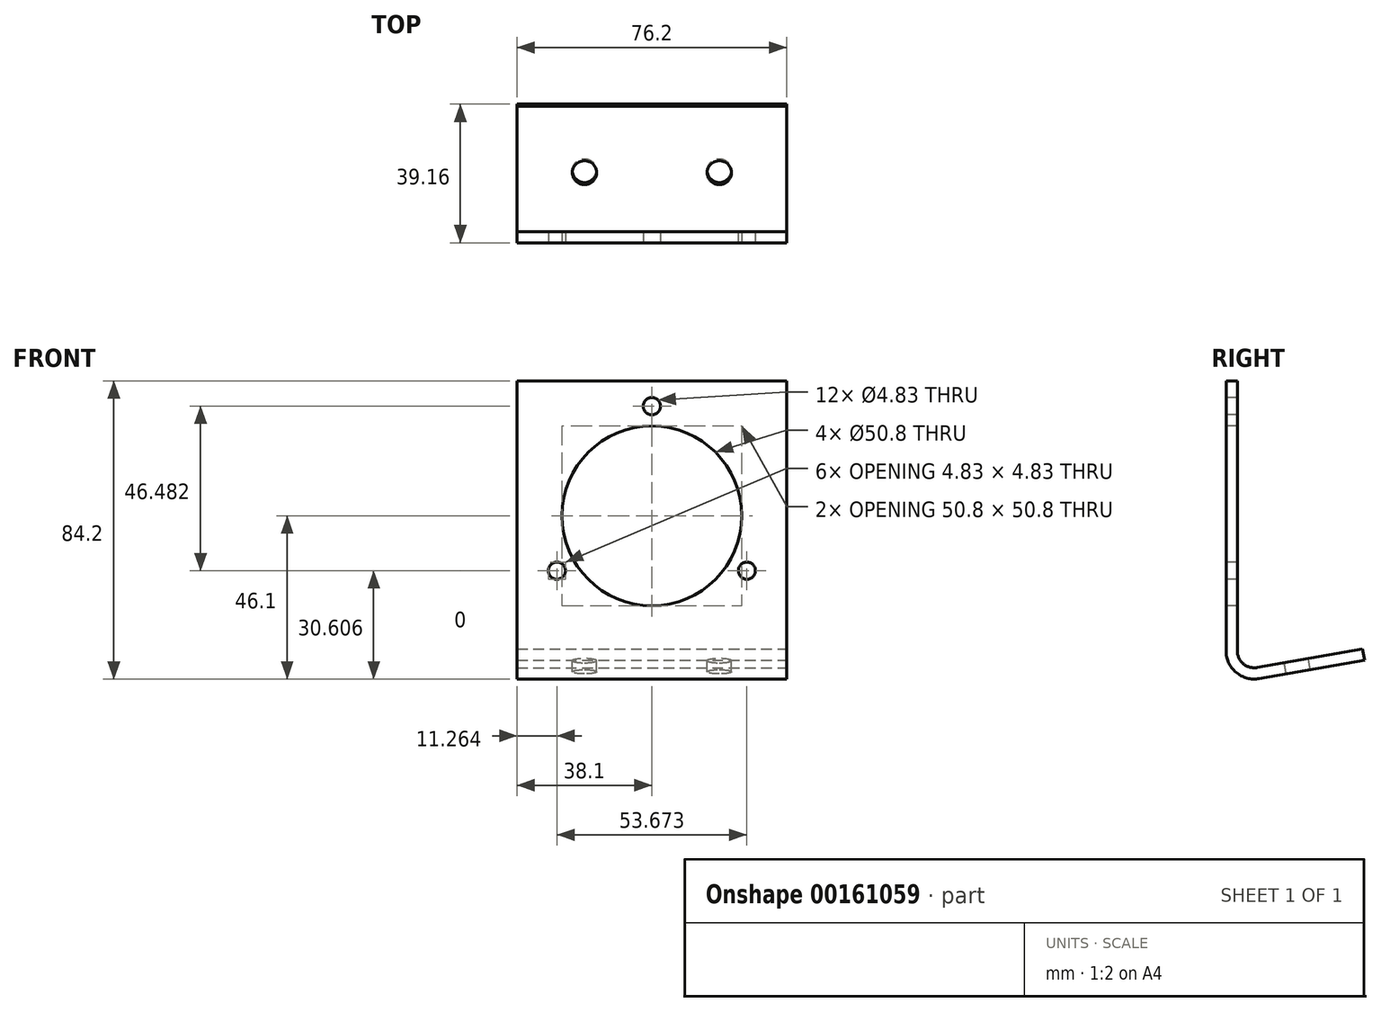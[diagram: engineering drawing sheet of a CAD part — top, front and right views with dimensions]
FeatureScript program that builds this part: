
annotation { "Feature Type Name" : "Feature", "Feature Type Description" : "" }
export const myFeature = defineFeature(function(context is Context, id is Id, definition is map)
    precondition{}
    {
        {
            var Q0;
            Q0=qCreatedBy(makeId("Right.planeOp"),FACE);
            var sketch = newSketch(context, id + "F0", { "sketchPlane" : qUnion([Q0])});
            skLineSegment(sketch, "E0", {"start": v(0, 0) * mm, "end": v(0, 76.2) * mm});
            skLineSegment(sketch, "E1", {"start": v(0, 76.2) * mm, "end": v(-3.18, 76.2) * mm});
            skLineSegment(sketch, "E2", {"start": v(0, 0) * mm, "end": v(0, 0) * mm});
            skLineSegment(sketch, "E3", {"start": v(5.66, -4.75) * mm, "end": v(35.43, 0.5) * mm});
            skPoint(sketch, "E4.visualSharp", {"position": v(0, -4.83) * mm});
            skArc(sketch, "E4.filletArc", {"start": v(0, 0) * mm, "mid": v(1.72, -3.7) * mm, "end": v(5.66, -4.75) * mm});
            skLineSegment(sketch, "E5.0", {"start": v(6.22, -7.88) * mm, "end": v(35.98, -2.63) * mm});
            skArc(sketch, "E5.1", {"start": v(-3.18, 0) * mm, "mid": v(-0.32, -6.13) * mm, "end": v(6.22, -7.88) * mm});
            skLineSegment(sketch, "E5.2", {"start": v(-3.18, 0) * mm, "end": v(-3.18, 76.2) * mm});
            skLineSegment(sketch, "E6", {"start": v(35.98, -2.63) * mm, "end": v(35.43, 0.5) * mm});
            skLineSegment(sketch, "E7", {"start": v(-3.18, 0) * mm, "end": v(-8.26, 28.87) * mm});
            skSolve(sketch);
        }
        {
            var Q0;
            Q0=makeQuery(id+"F0.imprint","IMPRINT",FACE,{"disambiguationData":[TD([[makeQuery(id+"F0.imprint","IMPRINT",EDGE,{"derivedFrom":sQuery(id+"F0.wireOp",EDGE,"E0")}),1.0]])]});
            extrude(context, id + "F1", {"entities" : qUnion([Q0]), "endBound" : BoundingType.SYMMETRIC, "oppositeDirection" : true, "depth" : 76.2 * mm});
        }
        {
            var Q0;
            Q0=makeQuery(id+"F1.opExtrude","SWEPT_FACE",FACE,{"disambiguationData":[OSD([sQuery(id+"F0.wireOp",EDGE,"E5.2")])]});
            var sketch = newSketch(context, id + "F2", { "sketchPlane" : qUnion([Q0])});
            skCircle(sketch, "E8", {"center": v(0, 38.1) * mm, "radius": 25.4 * mm});
            skCircle(sketch, "E9", {"center": v(0, 38.1) * mm, "radius": 30.99 * mm, "construction": true});
            skCircle(sketch, "E10", {"center": v(0, 69.09) * mm, "radius": 2.41 * mm});
            skCircle(sketch, "E11.1.0", {"center": v(-26.84, 22.6) * mm, "radius": 2.41 * mm});
            skCircle(sketch, "E11.2.0", {"center": v(26.84, 22.6) * mm, "radius": 2.41 * mm});
            skSolve(sketch);
        }
        {
            var Q0;
            Q0=makeQuery(id+"F2.imprint","IMPRINT",FACE,{"disambiguationData":[TD([[makeQuery(id+"F2.imprint","IMPRINT",EDGE,{"derivedFrom":sQuery(id+"F2.wireOp",EDGE,"E8")}),1.0]])]});
            var Q1;
            Q1=makeQuery(id+"F2.imprint","IMPRINT",FACE,{"disambiguationData":[TD([[makeQuery(id+"F2.imprint","IMPRINT",EDGE,{"derivedFrom":sQuery(id+"F2.wireOp",EDGE,"E11.1.0")}),1.0]])]});
            var Q2;
            Q2=makeQuery(id+"F2.imprint","IMPRINT",FACE,{"disambiguationData":[TD([[makeQuery(id+"F2.imprint","IMPRINT",EDGE,{"derivedFrom":sQuery(id+"F2.wireOp",EDGE,"E10")}),1.0]])]});
            var Q3;
            Q3=makeQuery(id+"F2.imprint","IMPRINT",FACE,{"disambiguationData":[TD([[makeQuery(id+"F2.imprint","IMPRINT",EDGE,{"derivedFrom":sQuery(id+"F2.wireOp",EDGE,"E11.2.0")}),1.0]])]});
            extrude(context, id + "F3", {"entities" : qUnion([Q0, Q1, Q2, Q3]), "operationType" : NewBodyOperationType.REMOVE, "oppositeDirection" : true, "depth" : 25.4 * mm});
        }
        {
            var Q0;
            Q0=makeQuery(id+"F1.opExtrude","SWEPT_FACE",FACE,{"disambiguationData":[OSD([sQuery(id+"F0.wireOp",EDGE,"E3")])]});
            var sketch = newSketch(context, id + "F4", { "sketchPlane" : qUnion([Q0])});
            skLineSegment(sketch, "E12", {"start": v(-38.1, 34.97) * mm, "end": v(-38.1, 15.92) * mm, "construction": true});
            skLineSegment(sketch, "E13", {"start": v(-38.1, 15.92) * mm, "end": v(-19.05, 15.92) * mm, "construction": true});
            skLineSegment(sketch, "E14", {"start": v(-19.05, 15.92) * mm, "end": v(19.05, 15.92) * mm, "construction": true});
            skCircle(sketch, "E15", {"center": v(19.05, 15.92) * mm, "radius": 3.43 * mm});
            skCircle(sketch, "E16", {"center": v(-19.05, 15.92) * mm, "radius": 3.43 * mm});
            skSolve(sketch);
        }
        {
            var Q0;
            Q0=makeQuery(id+"F4.imprint","IMPRINT",FACE,{"disambiguationData":[TD([[makeQuery(id+"F4.imprint","IMPRINT",EDGE,{"derivedFrom":sQuery(id+"F4.wireOp",EDGE,"E15")}),1.0]])]});
            var Q1;
            Q1=makeQuery(id+"F4.imprint","IMPRINT",FACE,{"disambiguationData":[TD([[makeQuery(id+"F4.imprint","IMPRINT",EDGE,{"derivedFrom":sQuery(id+"F4.wireOp",EDGE,"E16")}),1.0]])]});
            var Q2;
            Q2=sQuery(id+"F4.wireOp",EDGE,"E16");
            var Q3;
            Q3=sQuery(id+"F4.wireOp",EDGE,"E15");
            extrude(context, id + "F5", {"entities" : qUnion([Q0, Q1]), "operationType" : NewBodyOperationType.REMOVE, "surfaceEntities" : qUnion([Q2, Q3]), "oppositeDirection" : true, "depth" : 25.4 * mm});
        }
    });
